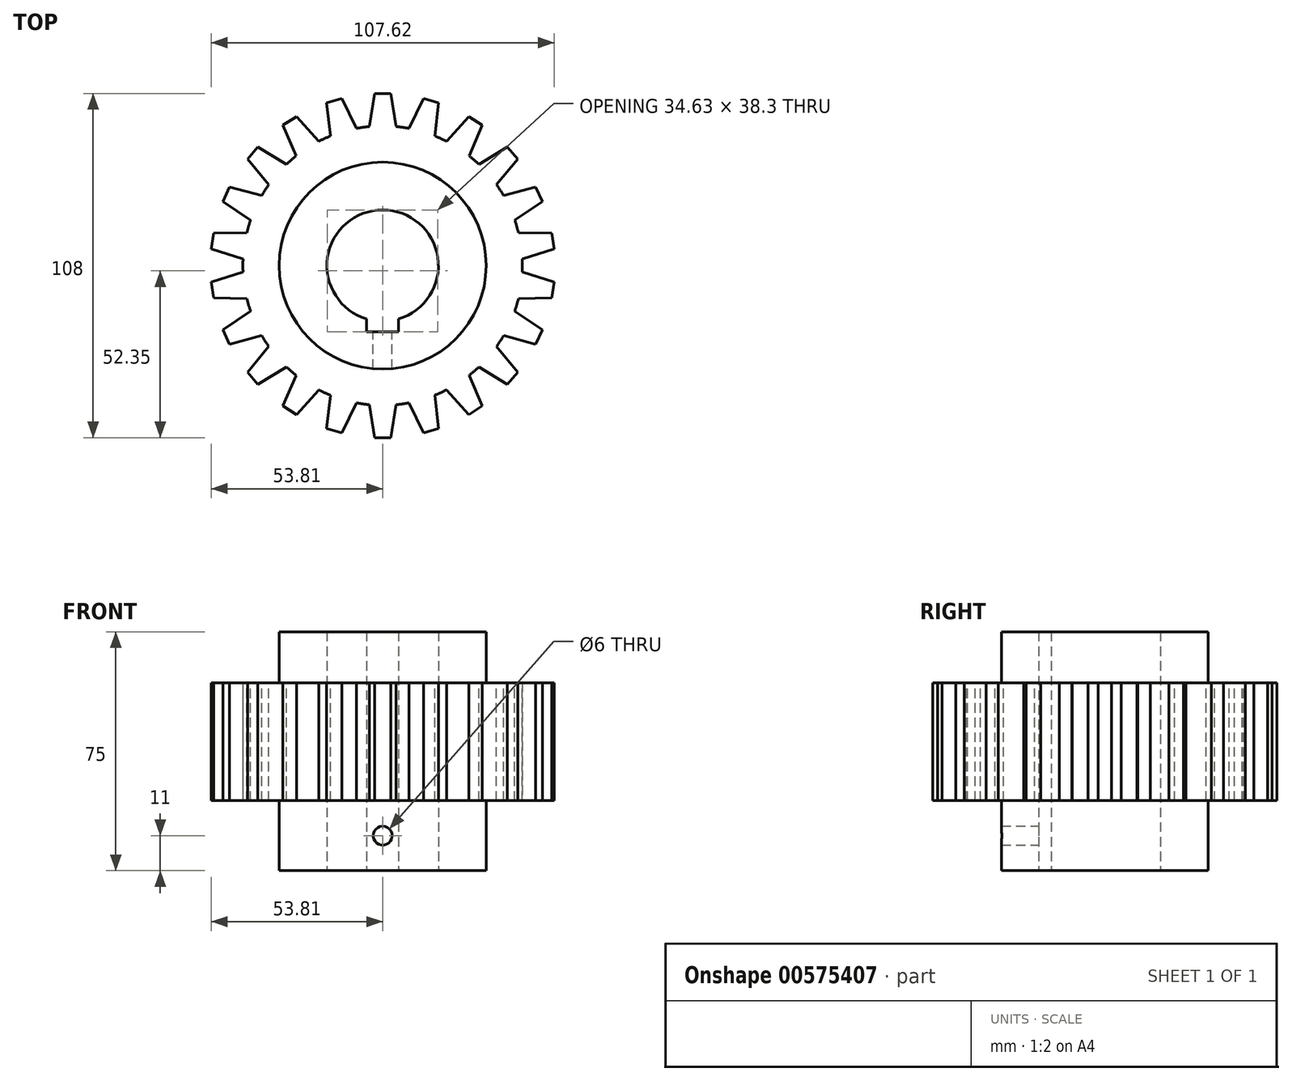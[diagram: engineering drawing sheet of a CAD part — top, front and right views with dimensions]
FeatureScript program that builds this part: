
annotation { "Feature Type Name" : "Feature", "Feature Type Description" : "" }
export const myFeature = defineFeature(function(context is Context, id is Id, definition is map)
    precondition{}
    {
        {
            var Q0;
            Q0=qCreatedBy(makeId("Top.planeOp"),FACE);
            var sketch = newSketch(context, id + "F0", { "sketchPlane" : qUnion([Q0])});
            skCircle(sketch, "E0", {"center": v(0, 0) * mm, "radius": 43.88 * mm});
            skSolve(sketch);
        }
        {
            var Q0;
            Q0=makeQuery(id+"F0.imprint","IMPRINT",FACE,{"disambiguationData":[TD([[makeQuery(id+"F0.imprint","IMPRINT",EDGE,{"derivedFrom":sQuery(id+"F0.wireOp",EDGE,"E0")}),1.0]])]});
            extrude(context, id + "F1", {"entities" : qUnion([Q0]), "depth" : 37 * mm, "offsetDistance" : 25 * mm});
        }
        {
            var Q0;
            Q0=makeQuery(id+"F1.opExtrude","CAP_FACE",FACE,{"disambiguationData":[OSD([sQuery(id+"F0.wireOp",EDGE,"E0")])],"isStart":false});
            var sketch = newSketch(context, id + "F2", { "sketchPlane" : qUnion([Q0])});
            skCircle(sketch, "E1.0", {"center": v(0, 0) * mm, "radius": 43.88 * mm});
            skLineSegment(sketch, "E2", {"start": v(-4.2, 43.67) * mm, "end": v(-2.5, 54) * mm});
            skLineSegment(sketch, "E3", {"start": v(-2.5, 54) * mm, "end": v(2.5, 54) * mm});
            skLineSegment(sketch, "E4", {"start": v(2.5, 54) * mm, "end": v(4.2, 43.67) * mm});
            skLineSegment(sketch, "E5", {"start": v(0, 54) * mm, "end": v(0, 0) * mm, "construction": true});
            skLineSegment(sketch, "E6", {"start": v(-4.2, 43.67) * mm, "end": v(0, 0) * mm, "construction": true});
            skLineSegment(sketch, "E7", {"start": v(0, 0) * mm, "end": v(4.2, 43.67) * mm, "construction": true});
            skSolve(sketch);
        }
        {
            var Q0;
            {var subQ0=sQuery(id+"F2.wireOp",EDGE,"E2");Q0=makeQuery(id+"F2.imprint","IMPRINT",FACE,{"disambiguationData":[TD([[makeQuery(id+"F2.imprint","IMPRINT",EDGE,{"derivedFrom":subQ0}),-1.0]])]});}
            var Q1;
            {var subQ0=sQuery(id+"F2.wireOp",EDGE,"E1.0");var subQ1=makeQuery(id+"F2.imprint","INTERSECT",VERTEX,{"derivedFrom":[subQ0,sQuery(id+"F2.wireOp",EDGE,"E2")]});Q1=makeQuery(id+"F2.imprint","IMPRINT",FACE,{"disambiguationData":[TD([[makeQuery(id+"F2.imprint","IMPRINT",EDGE,{"disambiguationData":[TD([[subQ1,1.0]])],"derivedFrom":subQ0}),1.0]])]});}
            var Q2;
            Q2=makeQuery(id+"F1.opExtrude","CAP_FACE",FACE,{"disambiguationData":[OSD([sQuery(id+"F0.wireOp",EDGE,"E0")])],"isStart":true});
            extrude(context, id + "F3", {"entities" : qUnion([Q0, Q1]), "operationType" : NewBodyOperationType.ADD, "endBound" : BoundingType.UP_TO_SURFACE, "oppositeDirection" : true, "depth" : 25 * mm, "endBoundEntityFace" : qUnion([Q2]), "offsetDistance" : 25 * mm});
        }
        {
            var Q0;
            Q0=qCreatedBy(makeId("Front.planeOp"),FACE);
            var sketch = newSketch(context, id + "F4", { "sketchPlane" : qUnion([Q0])});
            skLineSegment(sketch, "E8", {"start": v(0, 0) * mm, "end": v(0, 70) * mm, "construction": true});
            skSolve(sketch);
        }
        {
            var Q0;
            Q0=makeQuery(id+"F1.opExtrude","SWEPT_BODY",BODY,{"disambiguationData":[OSD([sQuery(id+"F0.wireOp",EDGE,"E0")])]});
            var Q1;
            Q1=sQuery(id+"F4.wireOp",EDGE,"E8");
            circularPattern(context, id + "F5", {"operationType" : NewBodyOperationType.ADD, "entities" : qUnion([Q0]), "axis" : qUnion([Q1]), "angle" : 360 * degree, "instanceCount" : 22, "equalSpace" : true});
        }
        {
            var Q0;
            {var subQ0=sQuery(id+"F0.wireOp",EDGE,"E0");var subQ1=makeQuery(id+"F3.boolean.opBoolean","MERGE",FACE,{"derivedFrom":[makeQuery(id+"F1.opExtrude","CAP_FACE",FACE,{"disambiguationData":[OSD([subQ0])],"isStart":true}),makeQuery(id+"F3.opExtrude","CAP_FACE",FACE,{"disambiguationData":[OSD([subQ0])],"isStart":false})]});Q0=makeQuery(id+"F5.boolean.opBoolean","MERGE",FACE,{"derivedFrom":[subQ1,makeQuery(id+"F5.opPattern","COPY",FACE,{"derivedFrom":subQ1,"instanceName":"1"}),makeQuery(id+"F5.opPattern","COPY",FACE,{"derivedFrom":subQ1,"instanceName":"2"}),makeQuery(id+"F5.opPattern","COPY",FACE,{"derivedFrom":subQ1,"instanceName":"3"}),makeQuery(id+"F5.opPattern","COPY",FACE,{"derivedFrom":subQ1,"instanceName":"4"}),makeQuery(id+"F5.opPattern","COPY",FACE,{"derivedFrom":subQ1,"instanceName":"5"}),makeQuery(id+"F5.opPattern","COPY",FACE,{"derivedFrom":subQ1,"instanceName":"6"}),makeQuery(id+"F5.opPattern","COPY",FACE,{"derivedFrom":subQ1,"instanceName":"7"}),makeQuery(id+"F5.opPattern","COPY",FACE,{"derivedFrom":subQ1,"instanceName":"8"}),makeQuery(id+"F5.opPattern","COPY",FACE,{"derivedFrom":subQ1,"instanceName":"9"}),makeQuery(id+"F5.opPattern","COPY",FACE,{"derivedFrom":subQ1,"instanceName":"10"}),makeQuery(id+"F5.opPattern","COPY",FACE,{"derivedFrom":subQ1,"instanceName":"11"}),makeQuery(id+"F5.opPattern","COPY",FACE,{"derivedFrom":subQ1,"instanceName":"12"}),makeQuery(id+"F5.opPattern","COPY",FACE,{"derivedFrom":subQ1,"instanceName":"13"}),makeQuery(id+"F5.opPattern","COPY",FACE,{"derivedFrom":subQ1,"instanceName":"14"}),makeQuery(id+"F5.opPattern","COPY",FACE,{"derivedFrom":subQ1,"instanceName":"15"}),makeQuery(id+"F5.opPattern","COPY",FACE,{"derivedFrom":subQ1,"instanceName":"16"}),makeQuery(id+"F5.opPattern","COPY",FACE,{"derivedFrom":subQ1,"instanceName":"17"}),makeQuery(id+"F5.opPattern","COPY",FACE,{"derivedFrom":subQ1,"instanceName":"18"}),makeQuery(id+"F5.opPattern","COPY",FACE,{"derivedFrom":subQ1,"instanceName":"19"}),makeQuery(id+"F5.opPattern","COPY",FACE,{"derivedFrom":subQ1,"instanceName":"20"}),makeQuery(id+"F5.opPattern","COPY",FACE,{"derivedFrom":subQ1,"instanceName":"21"})]});}
            var sketch = newSketch(context, id + "F6", { "sketchPlane" : qUnion([Q0])});
            skCircle(sketch, "E9", {"center": v(0, 0) * mm, "radius": 32.5 * mm});
            skSolve(sketch);
        }
        {
            var Q0;
            Q0=makeQuery(id+"F6.imprint","IMPRINT",FACE,{"disambiguationData":[TD([[makeQuery(id+"F6.imprint","IMPRINT",EDGE,{"derivedFrom":sQuery(id+"F6.wireOp",EDGE,"E9")}),1.0]])]});
            extrude(context, id + "F7", {"entities" : qUnion([Q0]), "operationType" : NewBodyOperationType.ADD, "depth" : 22 * mm, "offsetDistance" : 25 * mm});
        }
        {
            var Q0;
            Q0=makeQuery(id+"F7.opExtrude","CAP_FACE",FACE,{"disambiguationData":[OSD([sQuery(id+"F6.wireOp",EDGE,"E9")])],"isStart":false});
            var sketch = newSketch(context, id + "F8", { "sketchPlane" : qUnion([Q0])});
            skCircle(sketch, "E10", {"center": v(0, 0) * mm, "radius": 17.5 * mm});
            skLineSegment(sketch, "E11.bottom", {"start": v(-5, 20.8) * mm, "end": v(5, 20.8) * mm});
            skLineSegment(sketch, "E11.top", {"start": v(-5, 0) * mm, "end": v(5, 0) * mm});
            skLineSegment(sketch, "E11.left", {"start": v(-5, 20.8) * mm, "end": v(-5, 0) * mm});
            skLineSegment(sketch, "E11.right", {"start": v(5, 20.8) * mm, "end": v(5, 0) * mm});
            skPoint(sketch, "E11.middle", {"position": v(0, 10.4) * mm});
            skSolve(sketch);
        }
        {
            var Q0;
            {var subQ5=sQuery(id+"F8.wireOp",EDGE,"E11.top");Q0=makeQuery(id+"F8.imprint","IMPRINT",FACE,{"disambiguationData":[TD([[makeQuery(id+"F8.imprint","IMPRINT",EDGE,{"derivedFrom":subQ5}),1.0]])]});}
            var Q1;
            {var subQ5=sQuery(id+"F8.wireOp",EDGE,"E11.bottom");Q1=makeQuery(id+"F8.imprint","IMPRINT",FACE,{"disambiguationData":[TD([[makeQuery(id+"F8.imprint","IMPRINT",EDGE,{"derivedFrom":subQ5}),-1.0]])]});}
            var Q2;
            {var subQ5=sQuery(id+"F8.wireOp",EDGE,"E11.top");Q2=makeQuery(id+"F8.imprint","IMPRINT",FACE,{"disambiguationData":[TD([[makeQuery(id+"F8.imprint","IMPRINT",EDGE,{"derivedFrom":subQ5}),-1.0]])]});}
            extrude(context, id + "F9", {"entities" : qUnion([Q0, Q1, Q2]), "operationType" : NewBodyOperationType.REMOVE, "endBound" : BoundingType.THROUGH_ALL, "oppositeDirection" : true, "depth" : 25 * mm, "offsetDistance" : 25 * mm});
        }
        {
            var Q0;
            Q0=makeQuery(id+"F9.boolean.opBoolean","COPY",FACE,{"derivedFrom":makeQuery(id+"F9.opExtrude","SWEPT_FACE",FACE,{"disambiguationData":[OSD([sQuery(id+"F8.wireOp",EDGE,"E11.bottom")])]})});
            var sketch = newSketch(context, id + "F10", { "sketchPlane" : qUnion([Q0])});
            skCircle(sketch, "E12", {"center": v(0, -11) * mm, "radius": 3 * mm});
            skSolve(sketch);
        }
        {
            var Q0;
            Q0=makeQuery(id+"F10.imprint","IMPRINT",FACE,{"disambiguationData":[TD([[makeQuery(id+"F10.imprint","IMPRINT",EDGE,{"derivedFrom":sQuery(id+"F10.wireOp",EDGE,"E12")}),1.0]])]});
            extrude(context, id + "F11", {"entities" : qUnion([Q0]), "operationType" : NewBodyOperationType.REMOVE, "endBound" : BoundingType.THROUGH_ALL, "oppositeDirection" : true, "depth" : 25 * mm, "offsetDistance" : 25 * mm});
        }
        {
            var Q0;
            {var subQ0=makeQuery(id+"F3.boolean.opBoolean","MERGE",FACE,{"derivedFrom":[makeQuery(id+"F1.opExtrude","CAP_FACE",FACE,{"disambiguationData":[OSD([sQuery(id+"F0.wireOp",EDGE,"E0")])],"isStart":false}),makeQuery(id+"F3.opExtrude","CAP_FACE",FACE,{"disambiguationData":[OSD([sQuery(id+"F2.wireOp",EDGE,"E1.0"),sQuery(id+"F2.wireOp",EDGE,"E2"),sQuery(id+"F2.wireOp",EDGE,"E3"),sQuery(id+"F2.wireOp",EDGE,"E4")])],"isStart":true})]});Q0=makeQuery(id+"F5.boolean.opBoolean","MERGE",FACE,{"derivedFrom":[subQ0,makeQuery(id+"F5.opPattern","COPY",FACE,{"derivedFrom":subQ0,"instanceName":"1"}),makeQuery(id+"F5.opPattern","COPY",FACE,{"derivedFrom":subQ0,"instanceName":"2"}),makeQuery(id+"F5.opPattern","COPY",FACE,{"derivedFrom":subQ0,"instanceName":"3"}),makeQuery(id+"F5.opPattern","COPY",FACE,{"derivedFrom":subQ0,"instanceName":"4"}),makeQuery(id+"F5.opPattern","COPY",FACE,{"derivedFrom":subQ0,"instanceName":"5"}),makeQuery(id+"F5.opPattern","COPY",FACE,{"derivedFrom":subQ0,"instanceName":"6"}),makeQuery(id+"F5.opPattern","COPY",FACE,{"derivedFrom":subQ0,"instanceName":"7"}),makeQuery(id+"F5.opPattern","COPY",FACE,{"derivedFrom":subQ0,"instanceName":"8"}),makeQuery(id+"F5.opPattern","COPY",FACE,{"derivedFrom":subQ0,"instanceName":"9"}),makeQuery(id+"F5.opPattern","COPY",FACE,{"derivedFrom":subQ0,"instanceName":"10"}),makeQuery(id+"F5.opPattern","COPY",FACE,{"derivedFrom":subQ0,"instanceName":"11"}),makeQuery(id+"F5.opPattern","COPY",FACE,{"derivedFrom":subQ0,"instanceName":"12"}),makeQuery(id+"F5.opPattern","COPY",FACE,{"derivedFrom":subQ0,"instanceName":"13"}),makeQuery(id+"F5.opPattern","COPY",FACE,{"derivedFrom":subQ0,"instanceName":"14"}),makeQuery(id+"F5.opPattern","COPY",FACE,{"derivedFrom":subQ0,"instanceName":"15"}),makeQuery(id+"F5.opPattern","COPY",FACE,{"derivedFrom":subQ0,"instanceName":"16"}),makeQuery(id+"F5.opPattern","COPY",FACE,{"derivedFrom":subQ0,"instanceName":"17"}),makeQuery(id+"F5.opPattern","COPY",FACE,{"derivedFrom":subQ0,"instanceName":"18"}),makeQuery(id+"F5.opPattern","COPY",FACE,{"derivedFrom":subQ0,"instanceName":"19"}),makeQuery(id+"F5.opPattern","COPY",FACE,{"derivedFrom":subQ0,"instanceName":"20"}),makeQuery(id+"F5.opPattern","COPY",FACE,{"derivedFrom":subQ0,"instanceName":"21"})]});}
            var sketch = newSketch(context, id + "F12", { "sketchPlane" : qUnion([Q0])});
            skLineSegment(sketch, "E13.0.0", {"start": v(-2.5, 54) * mm, "end": v(-4.2, 43.67) * mm});
            skArc(sketch, "E13.0.1", {"start": v(-4.2, 43.67) * mm, "mid": v(-6.24, 43.43) * mm, "end": v(-8.27, 43.09) * mm});
            skLineSegment(sketch, "E13.0.2", {"start": v(-8.27, 43.09) * mm, "end": v(-12.81, 52.52) * mm});
            skLineSegment(sketch, "E13.0.3", {"start": v(-12.81, 52.52) * mm, "end": v(-17.61, 51.1) * mm});
            skLineSegment(sketch, "E13.0.4", {"start": v(-17.61, 51.1) * mm, "end": v(-16.34, 40.72) * mm});
            skArc(sketch, "E13.0.5", {"start": v(-16.34, 40.72) * mm, "mid": v(-18.23, 39.91) * mm, "end": v(-20.07, 39.01) * mm});
            skLineSegment(sketch, "E13.0.6", {"start": v(-20.07, 39.01) * mm, "end": v(-27.1, 46.78) * mm});
            skLineSegment(sketch, "E13.0.7", {"start": v(-27.1, 46.78) * mm, "end": v(-31.3, 44.08) * mm});
            skLineSegment(sketch, "E13.0.8", {"start": v(-31.3, 44.08) * mm, "end": v(-27.15, 34.47) * mm});
            skArc(sketch, "E13.0.9", {"start": v(-27.15, 34.47) * mm, "mid": v(-28.73, 33.16) * mm, "end": v(-30.25, 31.78) * mm});
            skLineSegment(sketch, "E13.0.10", {"start": v(-30.25, 31.78) * mm, "end": v(-39.17, 37.25) * mm});
            skLineSegment(sketch, "E13.0.11", {"start": v(-39.17, 37.25) * mm, "end": v(-42.45, 33.47) * mm});
            skLineSegment(sketch, "E13.0.12", {"start": v(-42.45, 33.47) * mm, "end": v(-35.76, 25.42) * mm});
            skArc(sketch, "E13.0.13", {"start": v(-35.76, 25.42) * mm, "mid": v(-36.9, 23.72) * mm, "end": v(-37.98, 21.97) * mm});
            skLineSegment(sketch, "E13.0.14", {"start": v(-37.98, 21.97) * mm, "end": v(-48.08, 24.7) * mm});
            skLineSegment(sketch, "E13.0.15", {"start": v(-48.08, 24.7) * mm, "end": v(-50.16, 20.16) * mm});
            skLineSegment(sketch, "E13.0.16", {"start": v(-50.16, 20.16) * mm, "end": v(-41.47, 14.32) * mm});
            skArc(sketch, "E13.0.17", {"start": v(-41.47, 14.32) * mm, "mid": v(-42.1, 12.36) * mm, "end": v(-42.63, 10.38) * mm});
            skLineSegment(sketch, "E13.0.18", {"start": v(-42.63, 10.38) * mm, "end": v(-53.1, 10.16) * mm});
            skLineSegment(sketch, "E13.0.19", {"start": v(-53.1, 10.16) * mm, "end": v(-53.8, 5.21) * mm});
            skLineSegment(sketch, "E13.0.20", {"start": v(-53.8, 5.21) * mm, "end": v(-43.83, 2.05) * mm});
            skArc(sketch, "E13.0.21", {"start": v(-43.83, 2.05) * mm, "mid": v(-43.88, 0) * mm, "end": v(-43.83, -2.05) * mm});
            skLineSegment(sketch, "E13.0.22", {"start": v(-43.83, -2.05) * mm, "end": v(-53.8, -5.21) * mm});
            skLineSegment(sketch, "E13.0.23", {"start": v(-53.8, -5.21) * mm, "end": v(-53.1, -10.16) * mm});
            skLineSegment(sketch, "E13.0.24", {"start": v(-53.1, -10.16) * mm, "end": v(-42.63, -10.38) * mm});
            skArc(sketch, "E13.0.25", {"start": v(-42.63, -10.38) * mm, "mid": v(-42.1, -12.36) * mm, "end": v(-41.47, -14.32) * mm});
            skLineSegment(sketch, "E13.0.26", {"start": v(-41.47, -14.32) * mm, "end": v(-50.16, -20.16) * mm});
            skLineSegment(sketch, "E13.0.27", {"start": v(-50.16, -20.16) * mm, "end": v(-48.08, -24.7) * mm});
            skLineSegment(sketch, "E13.0.28", {"start": v(-48.08, -24.7) * mm, "end": v(-37.98, -21.97) * mm});
            skArc(sketch, "E13.0.29", {"start": v(-37.98, -21.97) * mm, "mid": v(-36.9, -23.72) * mm, "end": v(-35.76, -25.42) * mm});
            skLineSegment(sketch, "E13.0.30", {"start": v(-35.76, -25.42) * mm, "end": v(-42.45, -33.47) * mm});
            skLineSegment(sketch, "E13.0.31", {"start": v(-42.45, -33.47) * mm, "end": v(-39.17, -37.25) * mm});
            skLineSegment(sketch, "E13.0.32", {"start": v(-39.17, -37.25) * mm, "end": v(-30.25, -31.78) * mm});
            skArc(sketch, "E13.0.33", {"start": v(-30.25, -31.78) * mm, "mid": v(-28.73, -33.16) * mm, "end": v(-27.15, -34.47) * mm});
            skLineSegment(sketch, "E13.0.34", {"start": v(-27.15, -34.47) * mm, "end": v(-31.3, -44.08) * mm});
            skLineSegment(sketch, "E13.0.35", {"start": v(-31.3, -44.08) * mm, "end": v(-27.1, -46.78) * mm});
            skLineSegment(sketch, "E13.0.36", {"start": v(-27.1, -46.78) * mm, "end": v(-20.07, -39.01) * mm});
            skArc(sketch, "E13.0.37", {"start": v(-20.07, -39.01) * mm, "mid": v(-18.23, -39.91) * mm, "end": v(-16.34, -40.72) * mm});
            skLineSegment(sketch, "E13.0.38", {"start": v(-16.34, -40.72) * mm, "end": v(-17.61, -51.1) * mm});
            skLineSegment(sketch, "E13.0.39", {"start": v(-17.61, -51.1) * mm, "end": v(-12.81, -52.52) * mm});
            skLineSegment(sketch, "E13.0.40", {"start": v(-12.81, -52.52) * mm, "end": v(-8.27, -43.09) * mm});
            skArc(sketch, "E13.0.41", {"start": v(-8.27, -43.09) * mm, "mid": v(-6.24, -43.43) * mm, "end": v(-4.2, -43.67) * mm});
            skLineSegment(sketch, "E13.0.42", {"start": v(-4.2, -43.67) * mm, "end": v(-2.5, -54) * mm});
            skLineSegment(sketch, "E13.0.43", {"start": v(-2.5, -54) * mm, "end": v(2.5, -54) * mm});
            skLineSegment(sketch, "E13.0.44", {"start": v(2.5, -54) * mm, "end": v(4.2, -43.67) * mm});
            skArc(sketch, "E13.0.45", {"start": v(4.2, -43.67) * mm, "mid": v(6.24, -43.43) * mm, "end": v(8.27, -43.09) * mm});
            skLineSegment(sketch, "E13.0.46", {"start": v(8.27, -43.09) * mm, "end": v(12.81, -52.52) * mm});
            skLineSegment(sketch, "E13.0.47", {"start": v(12.81, -52.52) * mm, "end": v(17.61, -51.1) * mm});
            skLineSegment(sketch, "E13.0.48", {"start": v(17.61, -51.1) * mm, "end": v(16.34, -40.72) * mm});
            skArc(sketch, "E13.0.49", {"start": v(16.34, -40.72) * mm, "mid": v(18.23, -39.91) * mm, "end": v(20.07, -39.01) * mm});
            skLineSegment(sketch, "E13.0.50", {"start": v(20.07, -39.01) * mm, "end": v(27.1, -46.78) * mm});
            skLineSegment(sketch, "E13.0.51", {"start": v(27.1, -46.78) * mm, "end": v(31.3, -44.08) * mm});
            skLineSegment(sketch, "E13.0.52", {"start": v(31.3, -44.08) * mm, "end": v(27.15, -34.47) * mm});
            skArc(sketch, "E13.0.53", {"start": v(27.15, -34.47) * mm, "mid": v(28.73, -33.16) * mm, "end": v(30.25, -31.78) * mm});
            skLineSegment(sketch, "E13.0.54", {"start": v(30.25, -31.78) * mm, "end": v(39.17, -37.25) * mm});
            skLineSegment(sketch, "E13.0.55", {"start": v(39.17, -37.25) * mm, "end": v(42.45, -33.47) * mm});
            skLineSegment(sketch, "E13.0.56", {"start": v(42.45, -33.47) * mm, "end": v(35.76, -25.42) * mm});
            skArc(sketch, "E13.0.57", {"start": v(35.76, -25.42) * mm, "mid": v(36.9, -23.72) * mm, "end": v(37.98, -21.97) * mm});
            skLineSegment(sketch, "E13.0.58", {"start": v(37.98, -21.97) * mm, "end": v(48.08, -24.7) * mm});
            skLineSegment(sketch, "E13.0.59", {"start": v(48.08, -24.7) * mm, "end": v(50.16, -20.16) * mm});
            skLineSegment(sketch, "E13.0.60", {"start": v(50.16, -20.16) * mm, "end": v(41.47, -14.32) * mm});
            skArc(sketch, "E13.0.61", {"start": v(41.47, -14.32) * mm, "mid": v(42.1, -12.36) * mm, "end": v(42.63, -10.38) * mm});
            skLineSegment(sketch, "E13.0.62", {"start": v(42.63, -10.38) * mm, "end": v(53.1, -10.16) * mm});
            skLineSegment(sketch, "E13.0.63", {"start": v(53.1, -10.16) * mm, "end": v(53.8, -5.21) * mm});
            skLineSegment(sketch, "E13.0.64", {"start": v(53.8, -5.21) * mm, "end": v(43.83, -2.05) * mm});
            skArc(sketch, "E13.0.65", {"start": v(43.83, -2.05) * mm, "mid": v(43.88, 0) * mm, "end": v(43.83, 2.05) * mm});
            skLineSegment(sketch, "E13.0.66", {"start": v(43.83, 2.05) * mm, "end": v(53.8, 5.21) * mm});
            skLineSegment(sketch, "E13.0.67", {"start": v(53.8, 5.21) * mm, "end": v(53.1, 10.16) * mm});
            skLineSegment(sketch, "E13.0.68", {"start": v(53.1, 10.16) * mm, "end": v(42.63, 10.38) * mm});
            skArc(sketch, "E13.0.69", {"start": v(42.63, 10.38) * mm, "mid": v(42.1, 12.36) * mm, "end": v(41.47, 14.32) * mm});
            skLineSegment(sketch, "E13.0.70", {"start": v(41.47, 14.32) * mm, "end": v(50.16, 20.16) * mm});
            skLineSegment(sketch, "E13.0.71", {"start": v(50.16, 20.16) * mm, "end": v(48.08, 24.7) * mm});
            skLineSegment(sketch, "E13.0.72", {"start": v(48.08, 24.7) * mm, "end": v(37.98, 21.97) * mm});
            skArc(sketch, "E13.0.73", {"start": v(37.98, 21.97) * mm, "mid": v(36.9, 23.72) * mm, "end": v(35.76, 25.42) * mm});
            skLineSegment(sketch, "E13.0.74", {"start": v(35.76, 25.42) * mm, "end": v(42.45, 33.47) * mm});
            skLineSegment(sketch, "E13.0.75", {"start": v(42.45, 33.47) * mm, "end": v(39.17, 37.25) * mm});
            skLineSegment(sketch, "E13.0.76", {"start": v(39.17, 37.25) * mm, "end": v(30.25, 31.78) * mm});
            skArc(sketch, "E13.0.77", {"start": v(30.25, 31.78) * mm, "mid": v(28.73, 33.16) * mm, "end": v(27.15, 34.47) * mm});
            skLineSegment(sketch, "E13.0.78", {"start": v(27.15, 34.47) * mm, "end": v(31.3, 44.08) * mm});
            skLineSegment(sketch, "E13.0.79", {"start": v(31.3, 44.08) * mm, "end": v(27.1, 46.78) * mm});
            skLineSegment(sketch, "E13.0.80", {"start": v(27.1, 46.78) * mm, "end": v(20.07, 39.01) * mm});
            skArc(sketch, "E13.0.81", {"start": v(20.07, 39.01) * mm, "mid": v(18.23, 39.91) * mm, "end": v(16.34, 40.72) * mm});
            skLineSegment(sketch, "E13.0.82", {"start": v(16.34, 40.72) * mm, "end": v(17.61, 51.1) * mm});
            skLineSegment(sketch, "E13.0.83", {"start": v(17.61, 51.1) * mm, "end": v(12.81, 52.52) * mm});
            skLineSegment(sketch, "E13.0.84", {"start": v(12.81, 52.52) * mm, "end": v(8.27, 43.09) * mm});
            skArc(sketch, "E13.0.85", {"start": v(8.27, 43.09) * mm, "mid": v(6.24, 43.43) * mm, "end": v(4.2, 43.67) * mm});
            skLineSegment(sketch, "E13.0.86", {"start": v(4.2, 43.67) * mm, "end": v(2.5, 54) * mm});
            skLineSegment(sketch, "E13.0.87", {"start": v(2.5, 54) * mm, "end": v(-2.5, 54) * mm});
            skCircle(sketch, "E14", {"center": v(0, 0) * mm, "radius": 32.5 * mm});
            skSolve(sketch);
        }
        {
            var Q0;
            Q0=makeQuery(id+"F12.imprint","IMPRINT",FACE,{"disambiguationData":[TD([[makeQuery(id+"F12.imprint","IMPRINT",EDGE,{"derivedFrom":sQuery(id+"F12.wireOp",EDGE,"E14")}),1.0]])]});
            extrude(context, id + "F13", {"entities" : qUnion([Q0]), "operationType" : NewBodyOperationType.ADD, "depth" : 16 * mm, "offsetDistance" : 25 * mm});
        }
    });
